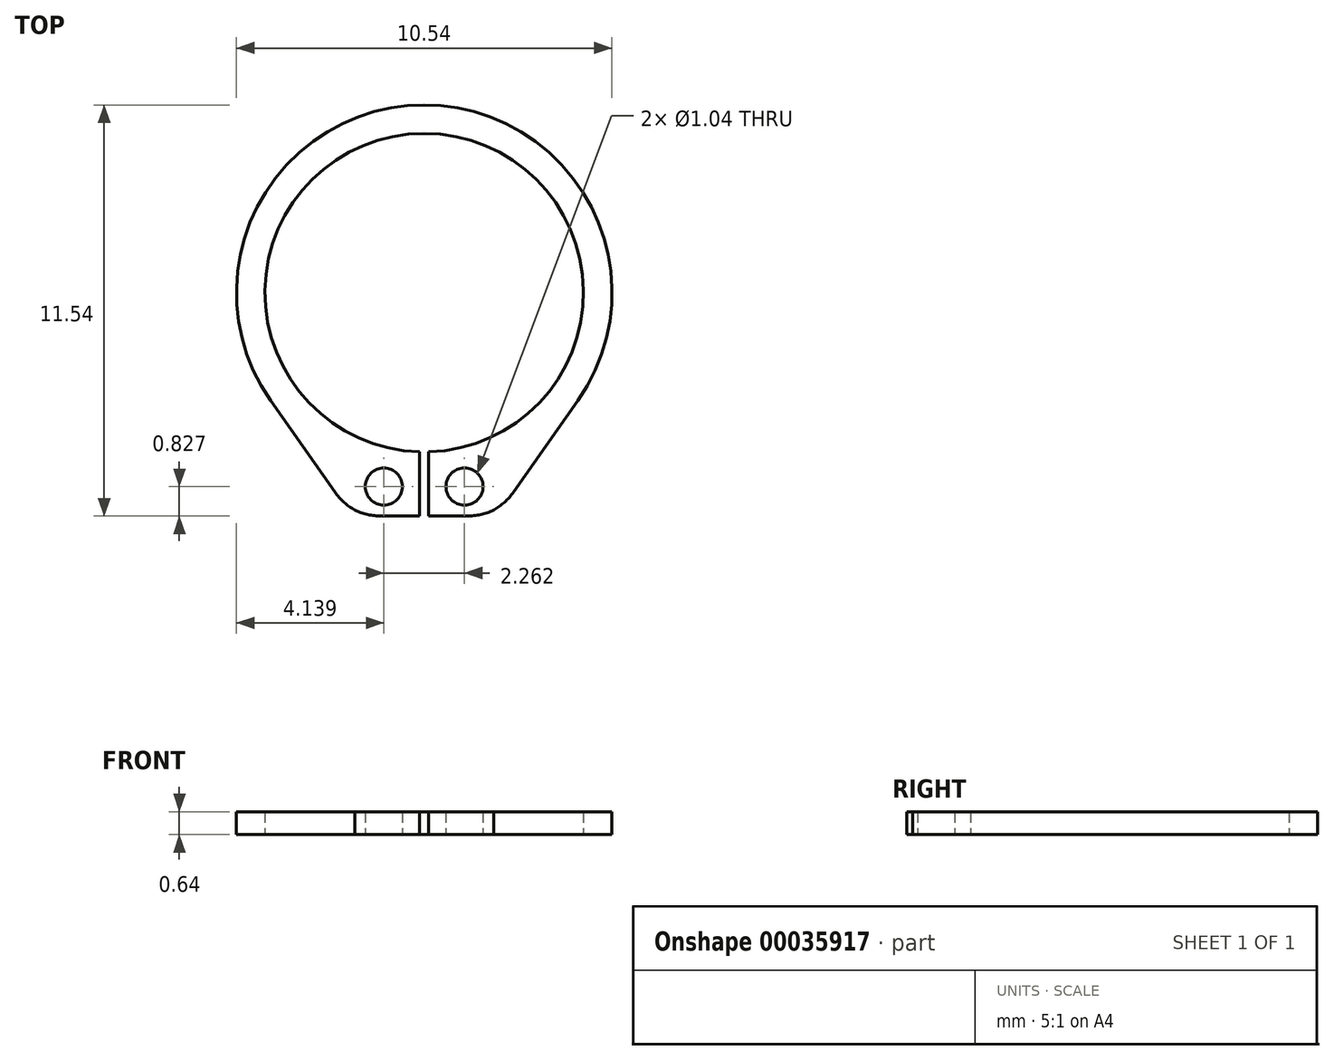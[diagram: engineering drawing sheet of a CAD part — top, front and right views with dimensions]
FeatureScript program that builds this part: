
annotation { "Feature Type Name" : "Feature", "Feature Type Description" : "" }
export const myFeature = defineFeature(function(context is Context, id is Id, definition is map)
    precondition{}
    {
        {
            var Q0;
            Q0=qCreatedBy(makeId("Top.planeOp"),FACE);
            var sketch = newSketch(context, id + "F0", { "sketchPlane" : qUnion([Q0])});
            skCircle(sketch, "E0", {"center": v(0, 0) * mm, "radius": 4.47 * mm});
            skCircle(sketch, "E1", {"center": v(0, 0) * mm, "radius": 5.27 * mm});
            skLineSegment(sketch, "E2", {"start": v(-0.13, -4.47) * mm, "end": v(-0.13, -5.27) * mm});
            skLineSegment(sketch, "E3", {"start": v(0.05, -4.47) * mm, "end": v(0.05, -5.27) * mm});
            skLineSegment(sketch, "E4.top", {"start": v(-0.13, -6.27) * mm, "end": v(-2.03, -6.27) * mm});
            skLineSegment(sketch, "E4.left", {"start": v(-0.13, -4.94) * mm, "end": v(-0.13, -6.27) * mm});
            skLineSegment(sketch, "E5", {"start": v(-2.03, -6.27) * mm, "end": v(-4.31, -3.03) * mm});
            skCircle(sketch, "E6", {"center": v(-1.13, -5.44) * mm, "radius": 0.52 * mm});
            skLineSegment(sketch, "E7", {"start": v(0, 4.47) * mm, "end": v(0, 5.27) * mm});
            skLineSegment(sketch, "E8", {"start": v(0, 0) * mm, "end": v(0, -4.94) * mm});
            skLineSegment(sketch, "E9", {"start": v(0, -4.94) * mm, "end": v(-0.13, -4.94) * mm});
            skSolve(sketch);
        }
        {
            var Q0;
            {var subQ6=sQuery(id+"F0.wireOp",EDGE,"E2");Q0=makeQuery(id+"F0.imprint","IMPRINT",FACE,{"disambiguationData":[TD([[makeQuery(id+"F0.imprint","IMPRINT",EDGE,{"derivedFrom":subQ6}),-1.0]])]});}
            var Q1;
            {var subQ7=sQuery(id+"F0.wireOp",EDGE,"E4.top");Q1=makeQuery(id+"F0.imprint","IMPRINT",FACE,{"disambiguationData":[TD([[makeQuery(id+"F0.imprint","IMPRINT",EDGE,{"derivedFrom":subQ7}),-1.0]])]});}
            extrude(context, id + "F1", {"entities" : qUnion([Q0, Q1]), "depth" : 0.64 * mm});
        }
        {
            var Q0;
            Q0=makeQuery(id+"F1.opExtrude","SWEPT_BODY",BODY,{"disambiguationData":[OSD([sQuery(id+"F0.wireOp",EDGE,"E0"),sQuery(id+"F0.wireOp",EDGE,"E1"),sQuery(id+"F0.wireOp",EDGE,"E2"),sQuery(id+"F0.wireOp",EDGE,"E4.top"),sQuery(id+"F0.wireOp",EDGE,"E4.left"),sQuery(id+"F0.wireOp",EDGE,"E5"),sQuery(id+"F0.wireOp",EDGE,"E6"),sQuery(id+"F0.wireOp",EDGE,"E7")])]});
            var Q1;
            Q1=qCreatedBy(makeId("Right.planeOp"),FACE);
            mirror(context, id + "F2", {"operationType" : NewBodyOperationType.ADD, "entities" : qUnion([Q0]), "mirrorPlane" : qUnion([Q1])});
        }
        {
            var Q0;
            Q0=makeQuery(id+"F1.opExtrude","SWEPT_EDGE",EDGE,{"disambiguationData":[OSD([sQuery(id+"F0.wireOp",EDGE,"E4.top"),sQuery(id+"F0.wireOp",EDGE,"E5")])]});
            var Q1;
            Q1=makeQuery(id+"F2.opPattern","COPY",EDGE,{"derivedFrom":makeQuery(id+"F1.opExtrude","SWEPT_EDGE",EDGE,{"disambiguationData":[OSD([sQuery(id+"F0.wireOp",EDGE,"E4.top"),sQuery(id+"F0.wireOp",EDGE,"E5")])]}),"instanceName":"1"});
            chamfer(context, id + "F3", {"entities" : qUnion([Q0, Q1]), "width" : 0.76 * mm, "tangentPropagation" : true});
        }
        {
            var Q0;
            {var subQ0=sQuery(id+"F0.wireOp",EDGE,"E4.top");Q0=makeQuery(id+"F3.opChamfer","BLEND_EDGE",EDGE,{"blendedFrom":[makeQuery(id+"F1.opExtrude","SWEPT_EDGE",EDGE,{"disambiguationData":[OSD([subQ0,sQuery(id+"F0.wireOp",EDGE,"E5")])]}),makeQuery(id+"F1.opExtrude","SWEPT_FACE",FACE,{"disambiguationData":[OSD([subQ0])]})],"blendedInto":[makeQuery(id+"F1.opExtrude","SWEPT_FACE",FACE,{"disambiguationData":[OSD([subQ0])]})]});}
            var Q1;
            {var subQ0=sQuery(id+"F0.wireOp",EDGE,"E5");Q1=makeQuery(id+"F3.opChamfer","BLEND_EDGE",EDGE,{"blendedFrom":[makeQuery(id+"F1.opExtrude","SWEPT_EDGE",EDGE,{"disambiguationData":[OSD([sQuery(id+"F0.wireOp",EDGE,"E4.top"),subQ0])]}),makeQuery(id+"F1.opExtrude","SWEPT_FACE",FACE,{"disambiguationData":[OSD([subQ0])]})],"blendedInto":[makeQuery(id+"F1.opExtrude","SWEPT_FACE",FACE,{"disambiguationData":[OSD([subQ0])]})]});}
            var Q2;
            {var subQ0=sQuery(id+"F0.wireOp",EDGE,"E4.top");Q2=makeQuery(id+"F3.opChamfer","BLEND_EDGE",EDGE,{"blendedFrom":[makeQuery(id+"F2.opPattern","COPY",EDGE,{"derivedFrom":makeQuery(id+"F1.opExtrude","SWEPT_EDGE",EDGE,{"disambiguationData":[OSD([subQ0,sQuery(id+"F0.wireOp",EDGE,"E5")])]}),"instanceName":"1"}),makeQuery(id+"F2.opPattern","COPY",FACE,{"derivedFrom":makeQuery(id+"F1.opExtrude","SWEPT_FACE",FACE,{"disambiguationData":[OSD([subQ0])]}),"instanceName":"1"})],"blendedInto":[makeQuery(id+"F2.opPattern","COPY",FACE,{"derivedFrom":makeQuery(id+"F1.opExtrude","SWEPT_FACE",FACE,{"disambiguationData":[OSD([subQ0])]}),"instanceName":"1"})]});}
            var Q3;
            {var subQ0=sQuery(id+"F0.wireOp",EDGE,"E5");Q3=makeQuery(id+"F3.opChamfer","BLEND_EDGE",EDGE,{"blendedFrom":[makeQuery(id+"F2.opPattern","COPY",EDGE,{"derivedFrom":makeQuery(id+"F1.opExtrude","SWEPT_EDGE",EDGE,{"disambiguationData":[OSD([sQuery(id+"F0.wireOp",EDGE,"E4.top"),subQ0])]}),"instanceName":"1"}),makeQuery(id+"F2.opPattern","COPY",FACE,{"derivedFrom":makeQuery(id+"F1.opExtrude","SWEPT_FACE",FACE,{"disambiguationData":[OSD([subQ0])]}),"instanceName":"1"})],"blendedInto":[makeQuery(id+"F2.opPattern","COPY",FACE,{"derivedFrom":makeQuery(id+"F1.opExtrude","SWEPT_FACE",FACE,{"disambiguationData":[OSD([subQ0])]}),"instanceName":"1"})]});}
            fillet(context, id + "F4", {"entities" : qUnion([Q0, Q1, Q2, Q3]), "radius" : 1.78 * mm, "tangentPropagation" : true, "allowEdgeOverflow" : false});
        }
    });
